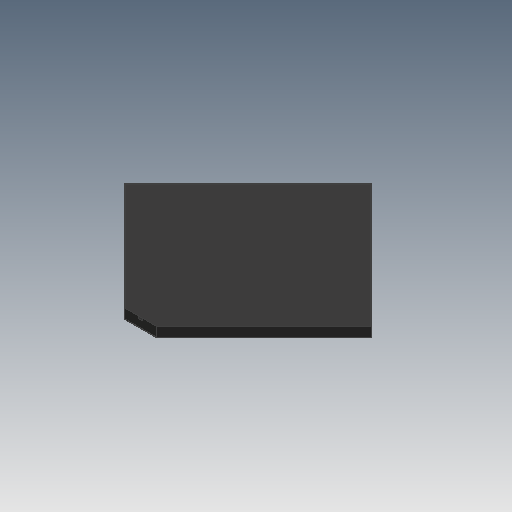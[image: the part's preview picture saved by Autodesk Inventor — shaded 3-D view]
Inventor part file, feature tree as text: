
AUTODESK INVENTOR PART (.ipt)
format: ipt  version: 2020 (Build 240168000, 168)  size: 120,320 bytes
history: native  units: mm
features: extrude x3, sketch x3, mirror x1
ambient origin geometry x8: Origin, YZ Plane, XZ Plane, XY Plane, X Axis, Y Axis, Z Axis, Center Point
bodies: Solid1 (feature_tree)
feature tree (7):
  extrude  "Extrusion1"  Depth=200.4mm
  extrude  "Extrusion3"  TaperAngle=0.0deg  [1 undecoded]
  extrude  "Extrusion2"  Depth=2.0mm
  mirror  "Mirror1"
  sketch  "Sketch1"  dims[d0=200.4mm d1=200.4mm]
  sketch  "Sketch2"  dims[d3=10.4mm d4=0.0mm]
  sketch  "Sketch4"  dims[d5=0.508mm d6=0.0mm d7=25.4mm d8=25.4mm d9=0.508mm d14=10.0mm d15=0.0mm d16=4.0mm d17=2.0mm]
note: 1 required parameter value undecoded (feature->parameter linkage not recoverable at this tier; creation-order binding heuristic only, values carry confidence <= 0.55)
